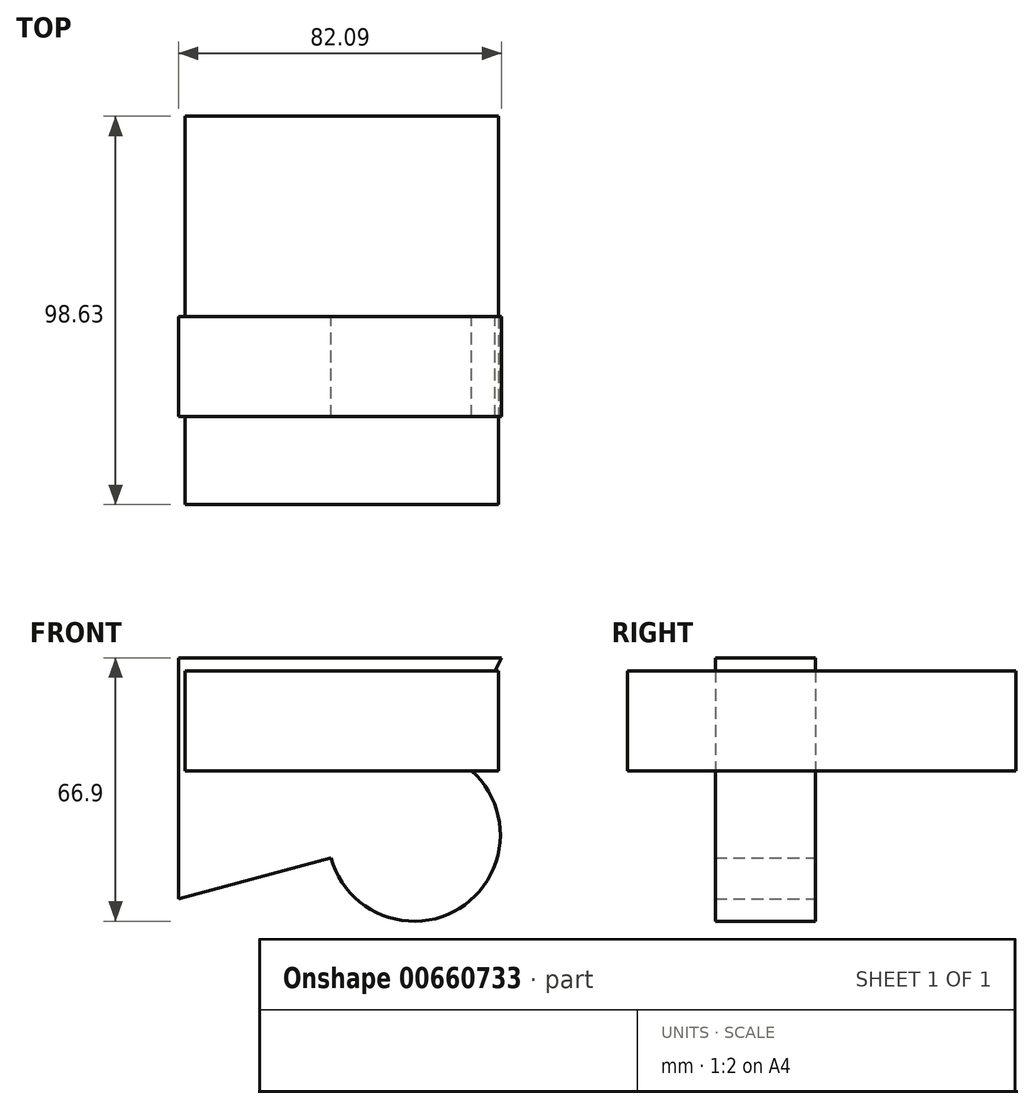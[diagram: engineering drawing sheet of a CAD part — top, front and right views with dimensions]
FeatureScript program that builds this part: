
annotation { "Feature Type Name" : "Feature", "Feature Type Description" : "" }
export const myFeature = defineFeature(function(context is Context, id is Id, definition is map)
    precondition{}
    {
        {
            var Q0;
            Q0=qCreatedBy(makeId("Front.planeOp"),FACE);
            var sketch = newSketch(context, id + "F0", { "sketchPlane" : qUnion([Q0])});
            skLineSegment(sketch, "E0", {"start": v(-38.24, 28.67) * mm, "end": v(43.85, 28.67) * mm});
            skLineSegment(sketch, "E1", {"start": v(43.85, 28.67) * mm, "end": v(-38.24, -32.6) * mm});
            skLineSegment(sketch, "E2", {"start": v(-38.24, -32.6) * mm, "end": v(-38.24, 28.67) * mm});
            skCircle(sketch, "E3", {"center": v(21.65, -16.35) * mm, "radius": 21.88 * mm});
            skLineSegment(sketch, "E4", {"start": v(43.85, 28.67) * mm, "end": v(21.65, -16.35) * mm});
            skLineSegment(sketch, "E5", {"start": v(-38.24, -32.6) * mm, "end": v(21.65, -16.35) * mm});
            skSolve(sketch);
        }
        {
            var Q0;
            Q0=qCreatedBy(makeId("Top.planeOp"),FACE);
            var sketch = newSketch(context, id + "F1", { "sketchPlane" : qUnion([Q0])});
            skLineSegment(sketch, "E6.bottom", {"start": v(-36.56, 50.94) * mm, "end": v(43.08, 50.94) * mm});
            skLineSegment(sketch, "E6.top", {"start": v(-36.56, -47.69) * mm, "end": v(43.08, -47.69) * mm});
            skLineSegment(sketch, "E6.left", {"start": v(-36.56, 50.94) * mm, "end": v(-36.56, -47.69) * mm});
            skLineSegment(sketch, "E6.right", {"start": v(43.08, 50.94) * mm, "end": v(43.08, -47.69) * mm});
            skSolve(sketch);
        }
        {
            var Q0;
            Q0=makeQuery(id+"F1.imprint","IMPRINT",FACE,{"disambiguationData":[TD([[makeQuery(id+"F1.imprint","IMPRINT",EDGE,{"derivedFrom":sQuery(id+"F1.wireOp",EDGE,"E6.bottom")}),-1.0]])]});
            extrude(context, id + "F2", {"entities" : qUnion([Q0]), "depth" : 25.4 * mm, "offsetDistance" : 25.4 * mm});
        }
        {
            var Q0;
            {var subQ0=sQuery(id+"F0.wireOp",EDGE,"E4");var subQ1=sQuery(id+"F0.wireOp",EDGE,"E3");var subQ2=makeQuery(id+"F0.imprint","INTERSECT",VERTEX,{"derivedFrom":[subQ1,subQ0]});Q0=makeQuery(id+"F0.imprint","IMPRINT",FACE,{"disambiguationData":[TD([[makeQuery(id+"F0.imprint","IMPRINT",EDGE,{"disambiguationData":[TD([[subQ2,1.0]])],"derivedFrom":subQ1}),1.0]])]});}
            var Q1;
            Q1 = qSketchRegion(id + "F0", true);
            var Q2;
            {var subQ0=sQuery(id+"F0.wireOp",EDGE,"E4");var subQ1=sQuery(id+"F0.wireOp",EDGE,"E3");var subQ2=makeQuery(id+"F0.imprint","INTERSECT",VERTEX,{"derivedFrom":[subQ1,subQ0]});Q2=makeQuery(id+"F0.imprint","IMPRINT",FACE,{"disambiguationData":[TD([[makeQuery(id+"F0.imprint","IMPRINT",EDGE,{"disambiguationData":[TD([[subQ2,-1.0]])],"derivedFrom":subQ1}),1.0]])]});}
            extrude(context, id + "F3", {"entities" : qUnion([Q0, Q1, Q2]), "operationType" : NewBodyOperationType.ADD, "depth" : 25.4 * mm, "offsetDistance" : 25.4 * mm});
        }
    });
